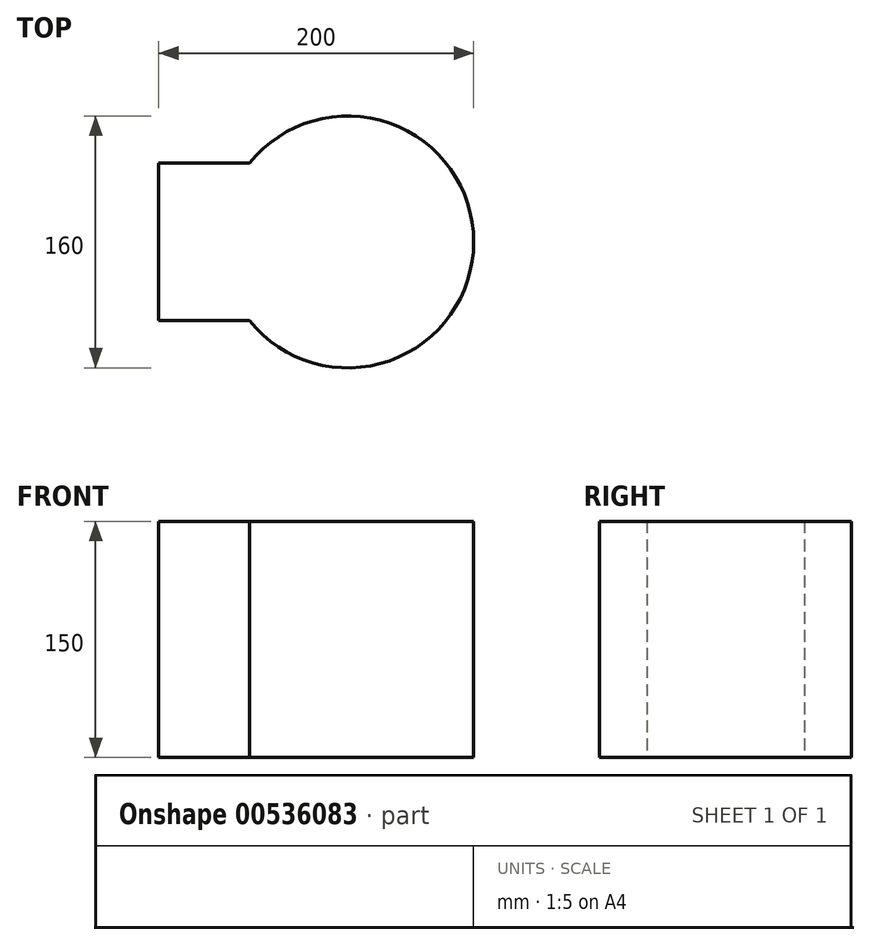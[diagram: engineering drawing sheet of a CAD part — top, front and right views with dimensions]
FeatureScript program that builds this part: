
annotation { "Feature Type Name" : "Feature", "Feature Type Description" : "" }
export const myFeature = defineFeature(function(context is Context, id is Id, definition is map)
    precondition{}
    {
        {
            var Q0;
            Q0=qCreatedBy(makeId("Top.planeOp"),FACE);
            var sketch = newSketch(context, id + "F0", { "sketchPlane" : qUnion([Q0])});
            skArc(sketch, "E0", {"start": v(-62.45, -50) * mm, "mid": v(80, 0) * mm, "end": v(-62.45, 50) * mm});
            skLineSegment(sketch, "E1", {"start": v(-62.45, 50) * mm, "end": v(-120, 50) * mm});
            skLineSegment(sketch, "E2", {"start": v(-120, 50) * mm, "end": v(-120, -50) * mm});
            skLineSegment(sketch, "E3", {"start": v(-120, -50) * mm, "end": v(-62.45, -50) * mm});
            skSolve(sketch);
        }
        {
            var Q0;
            Q0 = qSketchRegion(id + "F0", true);
            extrude(context, id + "F1", {"entities" : qUnion([Q0]), "depth" : 150 * mm, "offsetDistance" : 25 * mm});
        }
    });
